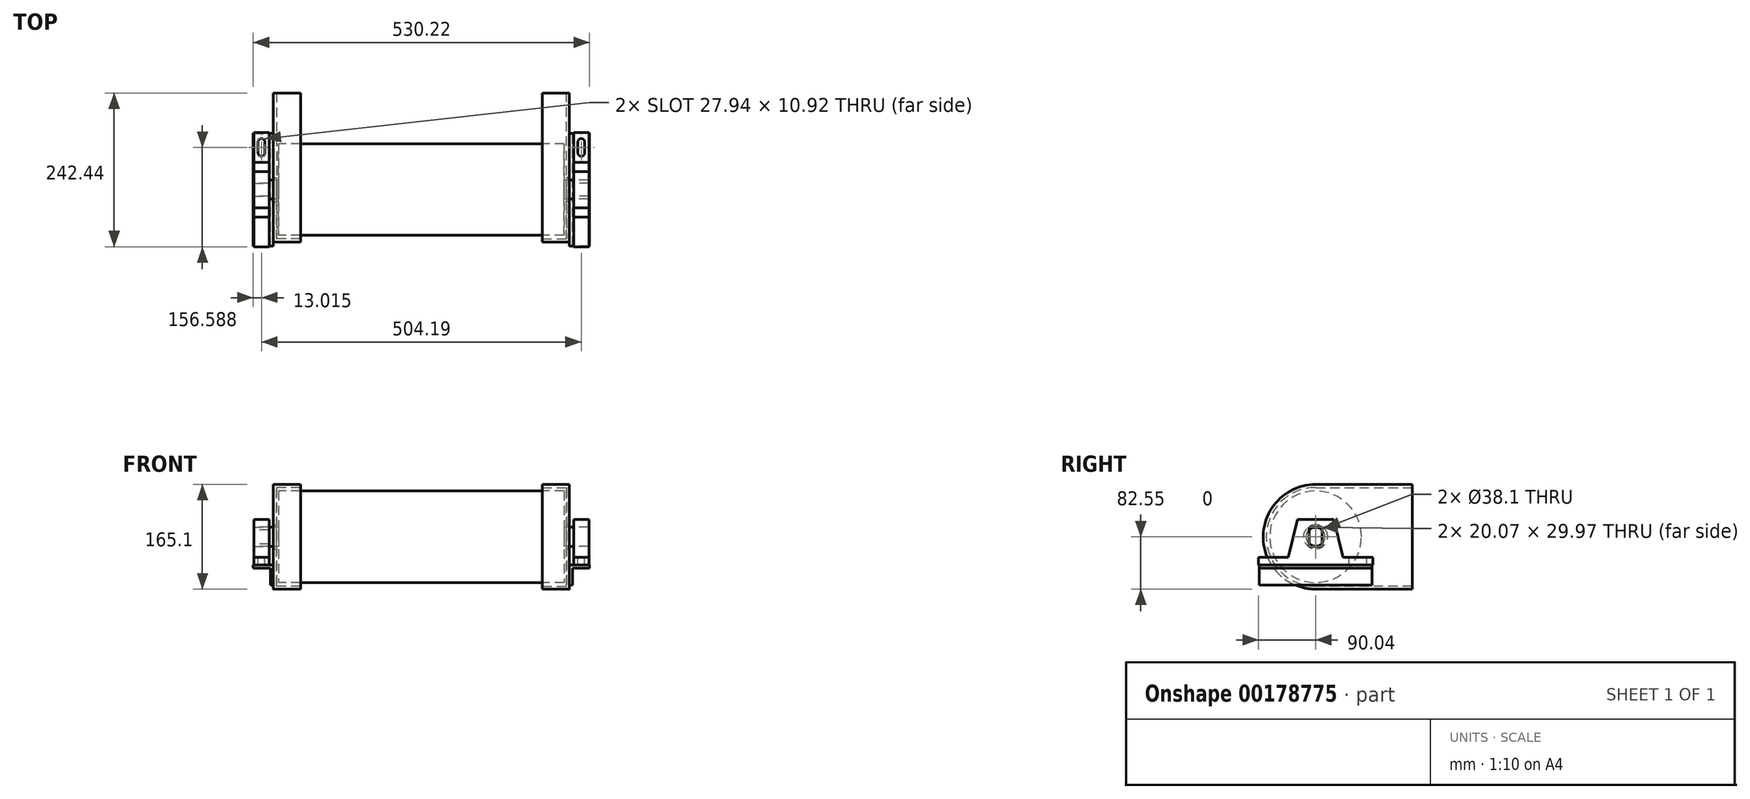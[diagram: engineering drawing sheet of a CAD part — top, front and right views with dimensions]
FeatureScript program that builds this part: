
annotation { "Feature Type Name" : "Feature", "Feature Type Description" : "" }
export const myFeature = defineFeature(function(context is Context, id is Id, definition is map)
    precondition{}
    {
        {
            var Q0;
            Q0=qCreatedBy(makeId("Front.planeOp"),FACE);
            var sketch = newSketch(context, id + "F0", { "sketchPlane" : qUnion([Q0])});
            skLineSegment(sketch, "E0.bottom", {"start": v(-225.04, 72.21) * mm, "end": v(225.04, 72.21) * mm});
            skLineSegment(sketch, "E0.left", {"start": v(-225.04, 72.21) * mm, "end": v(-225.04, 14.99) * mm});
            skLineSegment(sketch, "E0.right", {"start": v(225.04, 72.21) * mm, "end": v(225.04, 14.99) * mm});
            skLineSegment(sketch, "E1.bottom", {"start": v(-263.65, 14.99) * mm, "end": v(-225.04, 14.99) * mm});
            skLineSegment(sketch, "E1.left", {"start": v(-263.65, 14.99) * mm, "end": v(-263.65, 0) * mm});
            skLineSegment(sketch, "E2.bottom", {"start": v(225.04, 14.99) * mm, "end": v(263.65, 14.99) * mm});
            skLineSegment(sketch, "E2.right", {"start": v(263.65, 14.99) * mm, "end": v(263.65, 0) * mm});
            skLineSegment(sketch, "E3", {"start": v(-263.65, 0) * mm, "end": v(263.65, 0) * mm});
            skSolve(sketch);
        }
        {
            var Q0;
            Q0=makeQuery(id+"F0.imprint","IMPRINT",FACE,{"disambiguationData":[TD([[makeQuery(id+"F0.imprint","IMPRINT",EDGE,{"derivedFrom":sQuery(id+"F0.wireOp",EDGE,"E0.bottom")}),-1.0]])]});
            var Q1;
            Q1=sQuery(id+"F0.wireOp",EDGE,"E3");
            revolve(context, id + "F1", {"entities" : qUnion([Q0]), "axis" : qUnion([Q1]), "revolveType" : RevolveType.FULL});
        }
        {
            var Q0;
            Q0=makeQuery(id+"F1.opRevolve","SWEPT_FACE",FACE,{"disambiguationData":[OSD([sQuery(id+"F0.wireOp",EDGE,"E1.left")])]});
            var sketch = newSketch(context, id + "F2", { "sketchPlane" : qUnion([Q0])});
            skLineSegment(sketch, "E4.bottom", {"start": v(-10.03, 19.05) * mm, "end": v(10.03, 19.05) * mm});
            skLineSegment(sketch, "E4.top", {"start": v(-10.03, -19.05) * mm, "end": v(10.03, -19.05) * mm});
            skLineSegment(sketch, "E4.left", {"start": v(-10.03, 19.05) * mm, "end": v(-10.03, -19.05) * mm});
            skLineSegment(sketch, "E4.right", {"start": v(10.03, 19.05) * mm, "end": v(10.03, -19.05) * mm});
            skLineSegment(sketch, "E5.bottom", {"start": v(-22.73, 31.75) * mm, "end": v(22.73, 31.75) * mm});
            skLineSegment(sketch, "E5.top", {"start": v(-22.73, -31.75) * mm, "end": v(22.73, -31.75) * mm});
            skLineSegment(sketch, "E5.left", {"start": v(-22.73, 31.75) * mm, "end": v(-22.73, -31.75) * mm});
            skLineSegment(sketch, "E5.right", {"start": v(22.73, 31.75) * mm, "end": v(22.73, -31.75) * mm});
            skSolve(sketch);
        }
        {
            var Q0;
            {var subQ4=sQuery(id+"F2.wireOp",EDGE,"E4.bottom");Q0=makeQuery(id+"F2.imprint","IMPRINT",FACE,{"disambiguationData":[TD([[makeQuery(id+"F2.imprint","IMPRINT",EDGE,{"derivedFrom":subQ4}),1.0]])]});}
            var Q1;
            {var subQ0=sQuery(id+"F2.wireOp",EDGE,"E4.left");var subQ1=makeQuery(id+"F1.opRevolve","SWEPT_EDGE",EDGE,{"disambiguationData":[OSD([sQuery(id+"F0.wireOp",EDGE,"E1.bottom"),sQuery(id+"F0.wireOp",EDGE,"E1.left")])]});var subQ2=makeQuery(id+"F2.imprint","INTERSECT",VERTEX,{"disambiguationData":[OD(0.0)],"derivedFrom":[subQ1,subQ0]});Q1=makeQuery(id+"F2.imprint","IMPRINT",FACE,{"disambiguationData":[TD([[makeQuery(id+"F2.imprint","IMPRINT",EDGE,{"disambiguationData":[TD([[subQ2,-1.0]])],"derivedFrom":subQ0}),-1.0]])]});}
            var Q2;
            {var subQ0=sQuery(id+"F2.wireOp",EDGE,"E4.right");var subQ1=makeQuery(id+"F1.opRevolve","SWEPT_EDGE",EDGE,{"disambiguationData":[OSD([sQuery(id+"F0.wireOp",EDGE,"E1.bottom"),sQuery(id+"F0.wireOp",EDGE,"E1.left")])]});var subQ2=makeQuery(id+"F2.imprint","INTERSECT",VERTEX,{"disambiguationData":[OD(0.0)],"derivedFrom":[subQ1,subQ0]});Q2=makeQuery(id+"F2.imprint","IMPRINT",FACE,{"disambiguationData":[TD([[makeQuery(id+"F2.imprint","IMPRINT",EDGE,{"disambiguationData":[TD([[subQ2,-1.0]])],"derivedFrom":subQ0}),1.0]])]});}
            extrude(context, id + "F3", {"entities" : qUnion([Q0, Q1, Q2]), "operationType" : NewBodyOperationType.REMOVE, "oppositeDirection" : true, "depth" : 23.62 * mm});
        }
        {
            var Q0;
            Q0=qCreatedBy(makeId("Right.planeOp"),FACE);
            cPlane(context, id + "F4", {"entities" : qUnion([Q0]), "cplaneType" : CPlaneType.OFFSET, "offset" : 228.6 * mm, "width" : 152.4 * mm, "height" : 152.4 * mm});
        }
        {
            var Q0;
            Q0=qCreatedBy(id+"F4.planeOp",FACE);
            var sketch = newSketch(context, id + "F5", { "sketchPlane" : qUnion([Q0])});
            skArc(sketch, "E6", {"start": v(0, 82.55) * mm, "mid": v(-82.55, 0) * mm, "end": v(0, -82.55) * mm});
            skLineSegment(sketch, "E7", {"start": v(0, 82.55) * mm, "end": v(152.4, 82.55) * mm});
            skLineSegment(sketch, "E8", {"start": v(152.4, 82.55) * mm, "end": v(152.4, -82.55) * mm});
            skLineSegment(sketch, "E9", {"start": v(0, -82.55) * mm, "end": v(152.4, -82.55) * mm});
            skCircle(sketch, "E10", {"center": v(0, 0) * mm, "radius": 19.05 * mm});
            skSolve(sketch);
        }
        {
            var Q0;
            Q0=makeQuery(id+"F5.imprint","IMPRINT",FACE,{"disambiguationData":[TD([[makeQuery(id+"F5.imprint","IMPRINT",EDGE,{"derivedFrom":sQuery(id+"F5.wireOp",EDGE,"E6")}),1.0]])]});
            extrude(context, id + "F6", {"entities" : qUnion([Q0]), "operationType" : NewBodyOperationType.ADD, "depth" : 4.76 * mm});
        }
        {
            var Q0;
            Q0=makeQuery(id+"F6.opExtrude","CAP_FACE",FACE,{"disambiguationData":[OSD([sQuery(id+"F5.wireOp",EDGE,"E6"),sQuery(id+"F5.wireOp",EDGE,"E7"),sQuery(id+"F5.wireOp",EDGE,"E8"),sQuery(id+"F5.wireOp",EDGE,"E9"),sQuery(id+"F5.wireOp",EDGE,"E10")])],"isStart":true});
            var sketch = newSketch(context, id + "F7", { "sketchPlane" : qUnion([Q0])});
            skLineSegment(sketch, "E11.0.0", {"start": v(0, 82.55) * mm, "end": v(-152.4, 82.55) * mm});
            skLineSegment(sketch, "E11.0.1", {"start": v(-152.4, 82.55) * mm, "end": v(-152.4, -82.55) * mm});
            skLineSegment(sketch, "E11.0.2", {"start": v(-152.4, -82.55) * mm, "end": v(0, -82.55) * mm});
            skArc(sketch, "E11.0.3", {"start": v(0, -82.55) * mm, "mid": v(82.55, 0) * mm, "end": v(0, 82.55) * mm});
            skLineSegment(sketch, "E12.0", {"start": v(0, 77.79) * mm, "end": v(-152.4, 77.79) * mm});
            skArc(sketch, "E12.1", {"start": v(0, -77.79) * mm, "mid": v(77.79, 0) * mm, "end": v(0, 77.79) * mm});
            skLineSegment(sketch, "E12.2", {"start": v(-152.4, -77.79) * mm, "end": v(0, -77.79) * mm});
            skSolve(sketch);
        }
        {
            var Q0;
            {var subQ3=sQuery(id+"F7.wireOp",EDGE,"E11.0.0");Q0=makeQuery(id+"F7.imprint","IMPRINT",FACE,{"disambiguationData":[TD([[makeQuery(id+"F7.imprint","IMPRINT",EDGE,{"derivedFrom":subQ3}),1.0]])]});}
            extrude(context, id + "F8", {"entities" : qUnion([Q0]), "operationType" : NewBodyOperationType.ADD, "depth" : 38.1 * mm});
        }
        {
            var Q0;
            Q0=makeQuery(id+"F6.opExtrude","SWEPT_BODY",BODY,{"disambiguationData":[OSD([sQuery(id+"F5.wireOp",EDGE,"E6"),sQuery(id+"F5.wireOp",EDGE,"E7"),sQuery(id+"F5.wireOp",EDGE,"E8"),sQuery(id+"F5.wireOp",EDGE,"E9"),sQuery(id+"F5.wireOp",EDGE,"E10")])]});
            var Q1;
            Q1=qCreatedBy(makeId("Right.planeOp"),FACE);
            mirror(context, id + "F9", {"entities" : qUnion([Q0]), "mirrorPlane" : qUnion([Q1])});
        }
        {
            var Q0;
            {var subQ0=sQuery(id+"F2.wireOp",EDGE,"E4.right");Q0=makeQuery(id+"F3.boolean.opBoolean","COPY",FACE,{"disambiguationData":[TD([makeQuery(id+"F3.opExtrude","SWEPT_FACE",FACE,{"disambiguationData":[OSD([subQ0])]})])],"derivedFrom":makeQuery(id+"F3.opExtrude","CAP_FACE",FACE,{"disambiguationData":[OSD([sQuery(id+"F2.wireOp",EDGE,"E4.bottom"),sQuery(id+"F2.wireOp",EDGE,"E4.top"),sQuery(id+"F2.wireOp",EDGE,"E4.left"),subQ0,sQuery(id+"F2.wireOp",EDGE,"E5.bottom"),sQuery(id+"F2.wireOp",EDGE,"E5.top"),sQuery(id+"F2.wireOp",EDGE,"E5.left"),sQuery(id+"F2.wireOp",EDGE,"E5.right")])],"isStart":false})});}
            var sketch = newSketch(context, id + "F10", { "sketchPlane" : qUnion([Q0])});
            skLineSegment(sketch, "E13.0.0", {"start": v(-10.03, -14.99) * mm, "end": v(-10.03, 14.99) * mm});
            skArc(sketch, "E13.0.1", {"start": v(-10.03, -11.13) * mm, "mid": v(-14.99, 0) * mm, "end": v(-10.03, 11.13) * mm});
            skLineSegment(sketch, "E14.0.0", {"start": v(10.03, 14.99) * mm, "end": v(10.03, -14.99) * mm});
            skArc(sketch, "E14.0.1", {"start": v(10.03, 11.13) * mm, "mid": v(14.99, 0) * mm, "end": v(10.03, -11.13) * mm});
            skLineSegment(sketch, "E15", {"start": v(-10.03, 14.99) * mm, "end": v(10.03, 14.99) * mm});
            skLineSegment(sketch, "E16.top", {"start": v(-90.04, -44.45) * mm, "end": v(90.04, -44.45) * mm});
            skLineSegment(sketch, "E16.left", {"start": v(-90.04, -32.51) * mm, "end": v(-90.04, -44.45) * mm});
            skLineSegment(sketch, "E16.right", {"start": v(90.04, -32.51) * mm, "end": v(90.04, -44.45) * mm});
            skLineSegment(sketch, "E17", {"start": v(-43.05, -32.51) * mm, "end": v(-28.45, 27.43) * mm});
            skLineSegment(sketch, "E18", {"start": v(-28.45, 27.43) * mm, "end": v(28.45, 27.43) * mm});
            skLineSegment(sketch, "E19", {"start": v(28.45, 27.43) * mm, "end": v(43.05, -32.51) * mm});
            skLineSegment(sketch, "E20.trimOffspring", {"start": v(-10.03, -14.99) * mm, "end": v(10.03, -14.99) * mm});
            skLineSegment(sketch, "E21", {"start": v(-90.04, -32.51) * mm, "end": v(-43.05, -32.51) * mm});
            skLineSegment(sketch, "E22.trimOffspring", {"start": v(43.05, -32.51) * mm, "end": v(90.04, -32.51) * mm});
            skSolve(sketch);
        }
        {
            var Q0;
            {var subQ4=sQuery(id+"F10.wireOp",EDGE,"E13.0.1");Q0=makeQuery(id+"F10.imprint","IMPRINT",FACE,{"disambiguationData":[TD([[makeQuery(id+"F10.imprint","IMPRINT",EDGE,{"derivedFrom":subQ4}),1.0]])]});}
            var Q1;
            {var subQ0=sQuery(id+"F10.wireOp",EDGE,"E13.0.1");Q1=makeQuery(id+"F10.imprint","IMPRINT",FACE,{"disambiguationData":[TD([[makeQuery(id+"F10.imprint","IMPRINT",EDGE,{"derivedFrom":subQ0}),-1.0]])]});}
            var Q2;
            {var subQ0=sQuery(id+"F10.wireOp",EDGE,"E14.0.1");Q2=makeQuery(id+"F10.imprint","IMPRINT",FACE,{"disambiguationData":[TD([[makeQuery(id+"F10.imprint","IMPRINT",EDGE,{"derivedFrom":subQ0}),-1.0]])]});}
            extrude(context, id + "F11", {"entities" : qUnion([Q0, Q1, Q2]), "depth" : 24.13 * mm});
        }
        {
            var Q0;
            Q0=makeQuery(id+"F11.opExtrude","SWEPT_FACE",FACE,{"disambiguationData":[OSD([sQuery(id+"F10.wireOp",EDGE,"E21")])]});
            var sketch = newSketch(context, id + "F12", { "sketchPlane" : qUnion([Q0])});
            skArc(sketch, "E23", {"start": v(-246.63, 75.06) * mm, "mid": v(-252.1, 80.52) * mm, "end": v(-257.56, 75.06) * mm});
            skArc(sketch, "E24", {"start": v(-257.56, 58.04) * mm, "mid": v(-252.1, 52.58) * mm, "end": v(-246.63, 58.04) * mm});
            skLineSegment(sketch, "E25", {"start": v(-257.56, 75.06) * mm, "end": v(-257.56, 58.04) * mm});
            skLineSegment(sketch, "E26", {"start": v(-246.63, 58.04) * mm, "end": v(-246.63, 75.06) * mm});
            skSolve(sketch);
        }
        {
            var Q0;
            Q0=makeQuery(id+"F12.imprint","IMPRINT",FACE,{"disambiguationData":[TD([[makeQuery(id+"F12.imprint","IMPRINT",EDGE,{"derivedFrom":sQuery(id+"F12.wireOp",EDGE,"E23")}),1.0]])]});
            extrude(context, id + "F13", {"entities" : qUnion([Q0]), "operationType" : NewBodyOperationType.REMOVE, "endBound" : BoundingType.THROUGH_ALL, "oppositeDirection" : true, "depth" : 25.4 * mm});
        }
        {
            var Q0;
            Q0=makeQuery(id+"F11.opExtrude","SWEPT_BODY",BODY,{"disambiguationData":[OSD([sQuery(id+"F10.wireOp",EDGE,"E13.0.0"),sQuery(id+"F10.wireOp",EDGE,"E14.0.0"),sQuery(id+"F10.wireOp",EDGE,"E15"),sQuery(id+"F10.wireOp",EDGE,"E16.top"),sQuery(id+"F10.wireOp",EDGE,"E16.left"),sQuery(id+"F10.wireOp",EDGE,"E16.right"),sQuery(id+"F10.wireOp",EDGE,"E17"),sQuery(id+"F10.wireOp",EDGE,"E18"),sQuery(id+"F10.wireOp",EDGE,"E19"),sQuery(id+"F10.wireOp",EDGE,"E20.trimOffspring"),sQuery(id+"F10.wireOp",EDGE,"E21"),sQuery(id+"F10.wireOp",EDGE,"E22.trimOffspring")])]});
            var Q1;
            Q1=qCreatedBy(makeId("Right.planeOp"),FACE);
            mirror(context, id + "F14", {"entities" : qUnion([Q0]), "mirrorPlane" : qUnion([Q1])});
        }
        {
            var Q0;
            Q0=qCreatedBy(makeId("Front.planeOp"),FACE);
            var sketch = newSketch(context, id + "F15", { "sketchPlane" : qUnion([Q0])});
            skLineSegment(sketch, "E27", {"start": v(-265.11, -44.45) * mm, "end": v(-233.36, -44.45) * mm});
            skLineSegment(sketch, "E28", {"start": v(-233.36, -44.45) * mm, "end": v(-233.36, -76.2) * mm});
            skLineSegment(sketch, "E29.0", {"start": v(-265.11, -49.21) * mm, "end": v(-238.13, -49.21) * mm});
            skLineSegment(sketch, "E30.0", {"start": v(-238.13, -49.21) * mm, "end": v(-238.13, -76.2) * mm});
            skLineSegment(sketch, "E31", {"start": v(-265.11, -49.21) * mm, "end": v(-265.11, -44.45) * mm});
            skLineSegment(sketch, "E32", {"start": v(-238.13, -76.2) * mm, "end": v(-233.36, -76.2) * mm});
            skSolve(sketch);
        }
        {
            var Q0;
            Q0=makeQuery(id+"F15.imprint","IMPRINT",FACE,{"disambiguationData":[TD([[makeQuery(id+"F15.imprint","IMPRINT",EDGE,{"derivedFrom":sQuery(id+"F15.wireOp",EDGE,"E27")}),-1.0]])]});
            extrude(context, id + "F16", {"entities" : qUnion([Q0]), "endBound" : BoundingType.SYMMETRIC, "depth" : 177.8 * mm});
        }
        {
            var Q0;
            Q0=makeQuery(id+"F16.opExtrude","SWEPT_BODY",BODY,{"disambiguationData":[OSD([sQuery(id+"F15.wireOp",EDGE,"E27"),sQuery(id+"F15.wireOp",EDGE,"E28"),sQuery(id+"F15.wireOp",EDGE,"E29.0"),sQuery(id+"F15.wireOp",EDGE,"E30.0"),sQuery(id+"F15.wireOp",EDGE,"E31"),sQuery(id+"F15.wireOp",EDGE,"E32")])]});
            var Q1;
            Q1=qCreatedBy(makeId("Right.planeOp"),FACE);
            mirror(context, id + "F17", {"entities" : qUnion([Q0]), "mirrorPlane" : qUnion([Q1])});
        }
    });
